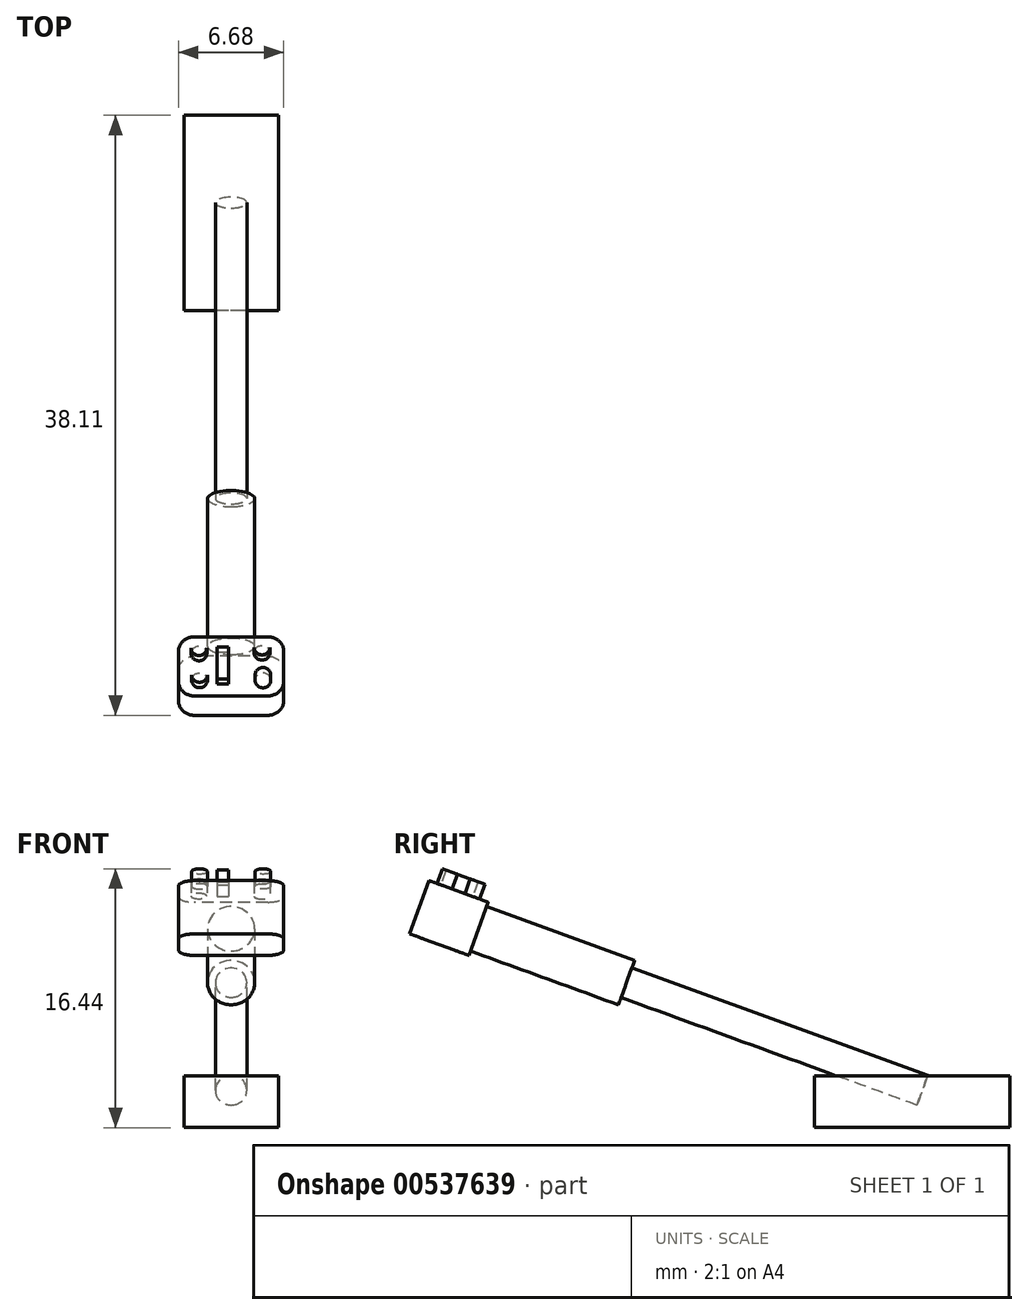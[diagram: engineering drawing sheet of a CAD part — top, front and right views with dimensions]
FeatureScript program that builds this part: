
annotation { "Feature Type Name" : "Feature", "Feature Type Description" : "" }
export const myFeature = defineFeature(function(context is Context, id is Id, definition is map)
    precondition{}
    {
        {
            var Q0;
            Q0=qCreatedBy(makeId("Front.planeOp"),FACE);
            var sketch = newSketch(context, id + "F0", { "sketchPlane" : qUnion([Q0])});
            skCircle(sketch, "E0", {"center": v(0, 0) * mm, "radius": 1 * mm});
            skSolve(sketch);
        }
        {
            var Q0;
            Q0=makeQuery(id+"F0.imprint","IMPRINT",FACE,{"disambiguationData":[TD([[makeQuery(id+"F0.imprint","IMPRINT",EDGE,{"derivedFrom":sQuery(id+"F0.wireOp",EDGE,"E0")}),1.0]])]});
            extrude(context, id + "F1", {"entities" : qUnion([Q0]), "oppositeDirection" : true, "depth" : 20 * mm, "offsetDistance" : 25 * mm});
        }
        {
            var Q0;
            Q0=qCreatedBy(makeId("Front.planeOp"),FACE);
            var sketch = newSketch(context, id + "F2", { "sketchPlane" : qUnion([Q0])});
            skCircle(sketch, "E1", {"center": v(0, 0) * mm, "radius": 1.5 * mm});
            skSolve(sketch);
        }
        {
            var Q0;
            Q0=makeQuery(id+"F2.imprint","IMPRINT",FACE,{"disambiguationData":[TD([[makeQuery(id+"F2.imprint","IMPRINT",EDGE,{"derivedFrom":sQuery(id+"F2.wireOp",EDGE,"E1")}),1.0]])]});
            extrude(context, id + "F3", {"entities" : qUnion([Q0]), "depth" : 10 * mm, "offsetDistance" : 25 * mm});
        }
        {
            var Q0;
            Q0=makeQuery(id+"F3.opExtrude","CAP_FACE",FACE,{"disambiguationData":[OSD([sQuery(id+"F2.wireOp",EDGE,"E1")])],"isStart":false});
            var sketch = newSketch(context, id + "F4", { "sketchPlane" : qUnion([Q0])});
            skLineSegment(sketch, "E2.bottom", {"start": v(3.34, -1.8) * mm, "end": v(-3.34, -1.8) * mm});
            skLineSegment(sketch, "E2.top", {"start": v(3.34, 1.8) * mm, "end": v(-3.34, 1.8) * mm});
            skLineSegment(sketch, "E2.left", {"start": v(3.34, -1.8) * mm, "end": v(3.34, 1.8) * mm});
            skLineSegment(sketch, "E2.right", {"start": v(-3.34, -1.8) * mm, "end": v(-3.34, 1.8) * mm});
            skPoint(sketch, "E2.middle", {"position": v(0, 0) * mm});
            skSolve(sketch);
        }
        {
            var Q0;
            Q0=makeQuery(id+"F4.imprint","IMPRINT",FACE,{"disambiguationData":[TD([[makeQuery(id+"F4.imprint","IMPRINT",EDGE,{"derivedFrom":sQuery(id+"F4.wireOp",EDGE,"E2.bottom")}),-1.0]])]});
            var Q1;
            Q1=makeQuery(id+"F4.imprint","IMPRINT",FACE,{"disambiguationData":[TD([[makeQuery(id+"F4.imprint","IMPRINT",EDGE,{"derivedFrom":makeQuery(id+"F3.opExtrude","CAP_EDGE",EDGE,{"disambiguationData":[OSD([sQuery(id+"F2.wireOp",EDGE,"E1")])],"isStart":false})}),1.0]])]});
            extrude(context, id + "F5", {"entities" : qUnion([Q0, Q1]), "operationType" : NewBodyOperationType.ADD, "depth" : 4 * mm, "offsetDistance" : 25 * mm});
        }
        {
            var Q0;
            Q0=makeQuery(id+"F5.opExtrude","CAP_EDGE",EDGE,{"disambiguationData":[OSD([sQuery(id+"F4.wireOp",EDGE,"E2.right")])],"isStart":true});
            var Q1;
            Q1=makeQuery(id+"F5.opExtrude","CAP_EDGE",EDGE,{"disambiguationData":[OSD([sQuery(id+"F4.wireOp",EDGE,"E2.right")])],"isStart":false});
            var Q2;
            Q2=makeQuery(id+"F5.opExtrude","CAP_EDGE",EDGE,{"disambiguationData":[OSD([sQuery(id+"F4.wireOp",EDGE,"E2.left")])],"isStart":false});
            var Q3;
            Q3=makeQuery(id+"F5.opExtrude","CAP_EDGE",EDGE,{"disambiguationData":[OSD([sQuery(id+"F4.wireOp",EDGE,"E2.left")])],"isStart":true});
            fillet(context, id + "F6", {"entities" : qUnion([Q0, Q1, Q2, Q3]), "tangentPropagation" : true, "radius" : 1 * mm, "defaultsChanged" : true, "vertexSettings" : [], "allowEdgeOverflow" : false});
        }
        {
            var Q0;
            Q0=makeQuery(id+"F5.opExtrude","SWEPT_FACE",FACE,{"disambiguationData":[OSD([sQuery(id+"F4.wireOp",EDGE,"E2.top")])]});
            var sketch = newSketch(context, id + "F7", { "sketchPlane" : qUnion([Q0])});
            skCircle(sketch, "E3", {"center": v(2.02, -12.95) * mm, "radius": 0.5 * mm});
            skCircle(sketch, "E4", {"center": v(1.96, -11.08) * mm, "radius": 0.5 * mm});
            skCircle(sketch, "E5", {"center": v(-2, -12.94) * mm, "radius": 0.5 * mm});
            skCircle(sketch, "E6", {"center": v(-2.04, -11.13) * mm, "radius": 0.5 * mm});
            skLineSegment(sketch, "E7.bottom", {"start": v(-0.9, -13.2) * mm, "end": v(-0.16, -13.2) * mm});
            skLineSegment(sketch, "E7.top", {"start": v(-0.9, -11.04) * mm, "end": v(-0.16, -11.04) * mm});
            skLineSegment(sketch, "E7.left", {"start": v(-0.9, -13.2) * mm, "end": v(-0.9, -11.04) * mm});
            skLineSegment(sketch, "E7.right", {"start": v(-0.16, -13.2) * mm, "end": v(-0.16, -11.04) * mm});
            skPoint(sketch, "E7.middle", {"position": v(0.68, -12.27) * mm});
            skSolve(sketch);
        }
        {
            var Q0;
            Q0=makeQuery(id+"F7.imprint","IMPRINT",FACE,{"disambiguationData":[TD([[makeQuery(id+"F7.imprint","IMPRINT",EDGE,{"derivedFrom":sQuery(id+"F7.wireOp",EDGE,"E4")}),1.0]])]});
            var Q1;
            Q1=makeQuery(id+"F7.imprint","IMPRINT",FACE,{"disambiguationData":[TD([[makeQuery(id+"F7.imprint","IMPRINT",EDGE,{"derivedFrom":sQuery(id+"F7.wireOp",EDGE,"E3")}),1.0]])]});
            var Q2;
            Q2=makeQuery(id+"F7.imprint","IMPRINT",FACE,{"disambiguationData":[TD([[makeQuery(id+"F7.imprint","IMPRINT",EDGE,{"derivedFrom":sQuery(id+"F7.wireOp",EDGE,"E6")}),1.0]])]});
            var Q3;
            Q3=makeQuery(id+"F7.imprint","IMPRINT",FACE,{"disambiguationData":[TD([[makeQuery(id+"F7.imprint","IMPRINT",EDGE,{"derivedFrom":sQuery(id+"F7.wireOp",EDGE,"E7.bottom")}),1.0]])]});
            var Q4;
            Q4=makeQuery(id+"F7.imprint","IMPRINT",FACE,{"disambiguationData":[TD([[makeQuery(id+"F7.imprint","IMPRINT",EDGE,{"derivedFrom":sQuery(id+"F7.wireOp",EDGE,"E5")}),1.0]])]});
            extrude(context, id + "F8", {"entities" : qUnion([Q0, Q1, Q2, Q3, Q4]), "operationType" : NewBodyOperationType.ADD, "depth" : 1 * mm, "offsetDistance" : 25 * mm});
        }
        {
            var Q0;
            Q0=makeQuery(id+"F1.opExtrude","SWEPT_BODY",BODY,{"disambiguationData":[OSD([sQuery(id+"F0.wireOp",EDGE,"E0")])]});
            var Q1;
            Q1=makeQuery(id+"F3.opExtrude","SWEPT_BODY",BODY,{"disambiguationData":[OSD([sQuery(id+"F2.wireOp",EDGE,"E1")])]});
            var Q2;
            Q2=makeQuery(id+"F5.opExtrude","CAP_EDGE",EDGE,{"disambiguationData":[OSD([sQuery(id+"F4.wireOp",EDGE,"E2.bottom")])],"isStart":true});
            transform(context, id + "F9", {"entities" : qUnion([Q0, Q1]), "transformType" : TransformType.ROTATION, "transformAxis" : qUnion([Q2]), "angle" : 20 * degree, "makeCopy" : false});
        }
        {
            var Q0;
            Q0=qCreatedBy(makeId("Right.planeOp"),FACE);
            var sketch = newSketch(context, id + "F10", { "sketchPlane" : qUnion([Q0])});
            skLineSegment(sketch, "E8.bottom", {"start": v(11.94, -12.74) * mm, "end": v(24.35, -12.74) * mm});
            skLineSegment(sketch, "E8.top", {"start": v(11.94, -9.44) * mm, "end": v(24.35, -9.44) * mm});
            skLineSegment(sketch, "E8.left", {"start": v(11.94, -12.74) * mm, "end": v(11.94, -9.44) * mm});
            skLineSegment(sketch, "E8.right", {"start": v(24.35, -12.74) * mm, "end": v(24.35, -9.44) * mm});
            skPoint(sketch, "E8.middle", {"position": v(18.14, -11.09) * mm});
            skSolve(sketch);
        }
        {
            var Q0;
            Q0=makeQuery(id+"F10.imprint","IMPRINT",FACE,{"disambiguationData":[TD([[makeQuery(id+"F10.imprint","IMPRINT",EDGE,{"derivedFrom":sQuery(id+"F10.wireOp",EDGE,"E8.bottom")}),1.0]])]});
            extrude(context, id + "F11", {"entities" : qUnion([Q0]), "depth" : 6 * mm, "offsetDistance" : 25 * mm, "symmetric" : true});
        }
    });
